# Revit family: XSoap_Dispenser-Sloan-Optima-BASYS-ESD-400_Series
name_source: partatom
category: Specialty Equipment
revit_build: Autodesk Revit 2014 (Build: 20130308_1515(x64)
units: mm (PartAtom-declared; Revit-internal decimal feet)

## types (4) — shared parameters
ADA Compliant = Yes
Assembly Code = E1090
Default Elevation = 0"
Description = Sensor Activated Electronic Soap Dispenser
Height = 4 13/32"
Installation Type = Deck Mounted
Length = 4 1/2"
Manufacturer = SLOAN
Operation = Sensor Activated
Price = Prices may vary. Please consult Manufacturer Representative for most up-to-date price list.
Product Documentation Link = https://specifications.sloan.com
Product Page URL = https://www.sloan.com
URL = https://www.sloan.com
Voltage = 120 V
Warranty Information = 3 Year Limited Warranty
Width = 2 1/4"

## per-type parameters (varying)
| type | Code Number | Finish | Material |
| ESD-400A CP | 3346080 | Metal-Sloan-Polished Chrome | Metal-Sloan-Polished Chrome |
| ESD-400A PVDBN | 3346081 | Metal-Sloan-Brushed Nickel | Metal-Sloan-Brushed Nickel |
| ESD-400A PVDPB | 3346083 | Metal-Sloan-Polished Brass | Metal-Sloan-Polished Brass |
| ESD-400A PVDSF | 3346082 | Metal-Sloan-Brushed Stainless | Metal-Sloan-Brushed Stainless |

note: column(s) folded — value = type name in every type: Model

## geometry (parser evidence)
native form markers: Sweep x1
no freeform markers — native parametric forms only
